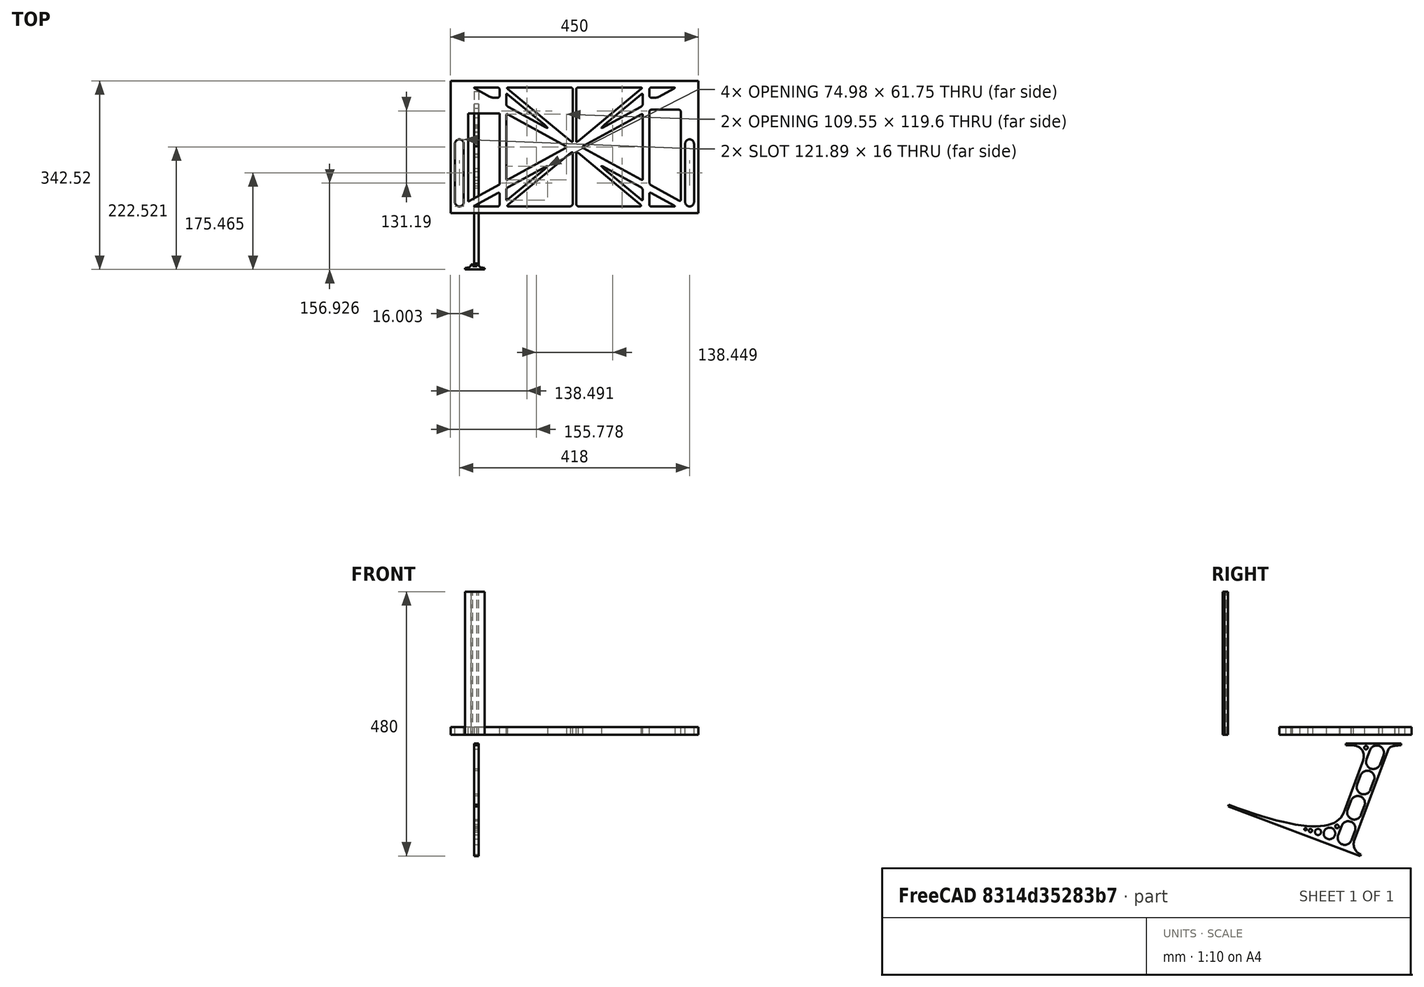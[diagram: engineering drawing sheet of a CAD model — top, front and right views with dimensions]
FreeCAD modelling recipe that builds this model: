
FCSTD DOCUMENT  (FreeCAD 0.19R0.19.2)
Label: laptopStand125FCStd
License: All rights reserved
LicenseURL: http://en.wikipedia.org/wiki/All_rights_reserved
objects: Sketcher::SketchObject×3, Part::Extrusion×3
note: 6 computed .brp shape members not serialized (recipe doc carries the construction recipe); baked Part::Feature solids carry a one-line shape summary decoded from their .brp

FEATURE [Sketcher::SketchObject] Sketch
  FullyConstrained = true
  sketch-geometry (351):
    g0: LineSegment StartX=-10.9272 StartY=-82.7794 StartZ=0 EndX=46.0728 EndY=-51.4823 EndZ=0
    g1: LineSegment StartX=-10.9272 StartY=77.3346 StartZ=0 EndX=-10.9272 EndY=-82.7794 EndZ=0
    g2: LineSegment StartX=46.0728 StartY=77.3346 StartZ=0 EndX=46.0728 EndY=-51.4823 EndZ=0
    g3: LineSegment StartX=-42.9272 StartY=136.221 StartZ=0 EndX=-42.9272 EndY=-103.779 EndZ=0
    g4: LineSegment StartX=407.073 StartY=136.221 StartZ=0 EndX=407.073 EndY=-103.779 EndZ=0
    g5: ArcOfCircle CenterX=-26.9272 CenterY=22.1087 CenterZ=0 NormalX=0 NormalY=0 NormalZ=1 AngleXU=0 Radius=8 StartAngle=1e-16 EndAngle=3.14159
    g6: ArcOfCircle CenterX=-26.9272 CenterY=-83.7794 CenterZ=0 NormalX=0 NormalY=0 NormalZ=1 AngleXU=0 Radius=8 StartAngle=3.14159 EndAngle=6.28319
    g7: LineSegment StartX=-34.9272 StartY=22.1087 StartZ=0 EndX=-34.9272 EndY=-83.7794 EndZ=0
    g8: LineSegment StartX=-18.9272 StartY=22.1087 StartZ=0 EndX=-18.9272 EndY=-83.7794 EndZ=0
    g9: ArcOfCircle CenterX=391.073 CenterY=22.1087 CenterZ=0 NormalX=0 NormalY=0 NormalZ=1 AngleXU=0 Radius=8 StartAngle=-4.4e-15 EndAngle=3.14159
    g10: LineSegment StartX=399.073 StartY=22.1087 StartZ=0 EndX=399.073 EndY=-83.7794 EndZ=0
    g11: LineSegment StartX=383.073 StartY=22.1087 StartZ=0 EndX=383.073 EndY=-83.7794 EndZ=0
    g12: ArcOfCircle CenterX=391.073 CenterY=-83.7794 CenterZ=0 NormalX=0 NormalY=0 NormalZ=1 AngleXU=0 Radius=8 StartAngle=3.14159 EndAngle=6.28319
    g13: Circle CenterX=175.022 CenterY=27.0628 CenterZ=0 NormalX=0 NormalY=0 NormalZ=1 AngleXU=0 Radius=1
    g14: Circle CenterX=179.022 CenterY=24.8665 CenterZ=0 NormalX=0 NormalY=0 NormalZ=1 AngleXU=0 Radius=1
    g15: Circle CenterX=179.022 CenterY=27.0628 CenterZ=0 NormalX=0 NormalY=0 NormalZ=1 AngleXU=0 Radius=1
    g16: BSplineCurve PolesCount=3 KnotsCount=2 Degree=2 IsPeriodic=0
    g17: GeomPoint X=175.022 Y=27.0628 Z=0
    g18: GeomPoint X=179.022 Y=27.0628 Z=0
    g19: Circle CenterX=189.124 CenterY=27.0628 CenterZ=0 NormalX=0 NormalY=0 NormalZ=1 AngleXU=0 Radius=1
    g20: Circle CenterX=185.124 CenterY=24.8665 CenterZ=0 NormalX=0 NormalY=0 NormalZ=1 AngleXU=0 Radius=1
    g21: Circle CenterX=185.124 CenterY=27.0628 CenterZ=0 NormalX=0 NormalY=0 NormalZ=1 AngleXU=0 Radius=1
    g22: BSplineCurve PolesCount=3 KnotsCount=2 Degree=2 IsPeriodic=0
    g23: GeomPoint X=189.124 Y=27.0628 Z=0
    g24: GeomPoint X=185.124 Y=27.0628 Z=0
    g25: Circle CenterX=175.022 CenterY=5.37834 CenterZ=0 NormalX=0 NormalY=0 NormalZ=1 AngleXU=0 Radius=1
    g26: Circle CenterX=179.022 CenterY=7.57463 CenterZ=0 NormalX=0 NormalY=0 NormalZ=1 AngleXU=0 Radius=1
    g27: Circle CenterX=179.022 CenterY=5.34704 CenterZ=0 NormalX=0 NormalY=0 NormalZ=1 AngleXU=0 Radius=1
    g28: BSplineCurve PolesCount=3 KnotsCount=2 Degree=2 IsPeriodic=0
    g29: GeomPoint X=175.022 Y=5.37834 Z=0
    g30: GeomPoint X=179.022 Y=5.34704 Z=0
    g31: Circle CenterX=189.124 CenterY=5.37834 CenterZ=0 NormalX=0 NormalY=0 NormalZ=1 AngleXU=0 Radius=1
    g32: Circle CenterX=185.124 CenterY=7.57463 CenterZ=0 NormalX=0 NormalY=0 NormalZ=1 AngleXU=0 Radius=1
    g33: Circle CenterX=185.124 CenterY=5.34704 CenterZ=0 NormalX=0 NormalY=0 NormalZ=1 AngleXU=0 Radius=1
    g34: BSplineCurve PolesCount=3 KnotsCount=2 Degree=2 IsPeriodic=0
    g35: GeomPoint X=189.124 Y=5.37834 Z=0
    g36: GeomPoint X=185.124 Y=5.34704 Z=0
    g37: Circle CenterX=165.871 CenterY=18.1458 CenterZ=0 NormalX=0 NormalY=0 NormalZ=1 AngleXU=0 Radius=1
    g38: Circle CenterX=169.377 CenterY=16.2206 CenterZ=0 NormalX=0 NormalY=0 NormalZ=1 AngleXU=0 Radius=1
    g39: Circle CenterX=165.871 CenterY=14.2954 CenterZ=0 NormalX=0 NormalY=0 NormalZ=1 AngleXU=0 Radius=1
    g40: BSplineCurve PolesCount=3 KnotsCount=2 Degree=2 IsPeriodic=0
    g41: GeomPoint X=165.871 Y=18.1458 Z=0
    g42: GeomPoint X=165.871 Y=14.2954 Z=0
    g43: Circle CenterX=198.275 CenterY=18.1458 CenterZ=0 NormalX=0 NormalY=0 NormalZ=1 AngleXU=0 Radius=1
    g44: Circle CenterX=194.768 CenterY=16.2206 CenterZ=0 NormalX=0 NormalY=0 NormalZ=1 AngleXU=0 Radius=1
    g45: Circle CenterX=198.275 CenterY=14.2954 CenterZ=0 NormalX=0 NormalY=0 NormalZ=1 AngleXU=0 Radius=1
    g46: BSplineCurve PolesCount=3 KnotsCount=2 Degree=2 IsPeriodic=0
    g47: GeomPoint X=198.275 Y=18.1458 Z=0
    g48: GeomPoint X=198.275 Y=14.2954 Z=0
    g49: LineSegment StartX=407.073 StartY=-103.779 StartZ=0 EndX=-42.9272 EndY=-103.779 EndZ=0
    g50: LineSegment StartX=407.073 StartY=136.221 StartZ=0 EndX=-42.9272 EndY=136.221 EndZ=0
    g51: LineSegment StartX=46.0728 StartY=77.3346 StartZ=0 EndX=-10.9272 EndY=77.3346 EndZ=0
    g52: Circle CenterX=125.607 CenterY=54.1951 CenterZ=0 NormalX=0 NormalY=0 NormalZ=1 AngleXU=0 Radius=1
    g53: Circle CenterX=139.632 CenterY=46.4944 CenterZ=0 NormalX=0 NormalY=0 NormalZ=1 AngleXU=0 Radius=1
    g54: Circle CenterX=127.326 CenterY=56.7187 CenterZ=0 NormalX=0 NormalY=0 NormalZ=1 AngleXU=0 Radius=1
    g55: BSplineCurve PolesCount=3 KnotsCount=2 Degree=2 IsPeriodic=0
    g56: GeomPoint X=125.607 Y=54.1951 Z=0
    g57: GeomPoint X=127.326 Y=56.7187 Z=0
    g58: Circle CenterX=236.821 CenterY=56.7187 CenterZ=0 NormalX=0 NormalY=0 NormalZ=1 AngleXU=0 Radius=1
    g59: Circle CenterX=224.513 CenterY=46.4944 CenterZ=0 NormalX=0 NormalY=0 NormalZ=1 AngleXU=0 Radius=1
    g60: Circle CenterX=238.538 CenterY=54.1951 CenterZ=0 NormalX=0 NormalY=0 NormalZ=1 AngleXU=0 Radius=1
    g61: BSplineCurve PolesCount=3 KnotsCount=2 Degree=2 IsPeriodic=0
    g62: GeomPoint X=236.821 Y=56.7187 Z=0
    g63: GeomPoint X=238.538 Y=54.1951 Z=0
    g64: Circle CenterX=238.538 CenterY=-21.7539 CenterZ=0 NormalX=0 NormalY=0 NormalZ=1 AngleXU=0 Radius=1
    g65: Circle CenterX=224.513 CenterY=-14.0532 CenterZ=0 NormalX=0 NormalY=0 NormalZ=1 AngleXU=0 Radius=1
    g66: Circle CenterX=236.821 CenterY=-24.2775 CenterZ=0 NormalX=0 NormalY=0 NormalZ=1 AngleXU=0 Radius=1
    g67: BSplineCurve PolesCount=3 KnotsCount=2 Degree=2 IsPeriodic=0
    g68: GeomPoint X=238.538 Y=-21.7539 Z=0
    g69: GeomPoint X=236.821 Y=-24.2775 Z=0
    g70: Circle CenterX=125.607 CenterY=-21.7539 CenterZ=0 NormalX=0 NormalY=0 NormalZ=1 AngleXU=0 Radius=1
    g71: Circle CenterX=139.632 CenterY=-14.0532 CenterZ=0 NormalX=0 NormalY=0 NormalZ=1 AngleXU=0 Radius=1
    g72: Circle CenterX=127.325 CenterY=-24.2775 CenterZ=0 NormalX=0 NormalY=0 NormalZ=1 AngleXU=0 Radius=1
    g73: BSplineCurve PolesCount=3 KnotsCount=2 Degree=2 IsPeriodic=0
    g74: GeomPoint X=125.607 Y=-21.7539 Z=0
    g75: GeomPoint X=127.325 Y=-24.2775 Z=0
    g76: Circle CenterX=302.996 CenterY=111.695 CenterZ=0 NormalX=0 NormalY=0 NormalZ=1 AngleXU=0 Radius=1
    g77: Circle CenterX=306.073 CenterY=114.251 CenterZ=0 NormalX=0 NormalY=0 NormalZ=1 AngleXU=0 Radius=1
    g78: Circle CenterX=306.073 CenterY=110.251 CenterZ=0 NormalX=0 NormalY=0 NormalZ=1 AngleXU=0 Radius=1
    g79: BSplineCurve PolesCount=3 KnotsCount=2 Degree=2 IsPeriodic=0
    g80: GeomPoint X=302.996 Y=111.695 Z=0
    g81: GeomPoint X=306.073 Y=110.251 Z=0
    g82: Circle CenterX=306.073 CenterY=95.2763 CenterZ=0 NormalX=0 NormalY=0 NormalZ=1 AngleXU=0 Radius=1
    g83: Circle CenterX=306.073 CenterY=91.2763 CenterZ=0 NormalX=0 NormalY=0 NormalZ=1 AngleXU=0 Radius=1
    g84: Circle CenterX=302.567 CenterY=89.3511 CenterZ=0 NormalX=0 NormalY=0 NormalZ=1 AngleXU=0 Radius=1
    g85: BSplineCurve PolesCount=3 KnotsCount=2 Degree=2 IsPeriodic=0
    g86: GeomPoint X=306.073 Y=95.2763 Z=0
    g87: GeomPoint X=302.567 Y=89.3511 Z=0
    g88: LineSegment StartX=306.073 StartY=110.251 StartZ=0 EndX=306.073 EndY=95.2763 EndZ=0
    g89: LineSegment StartX=302.996 StartY=111.695 StartZ=0 EndX=236.821 EndY=56.7187 EndZ=0
    g90: LineSegment StartX=238.538 StartY=54.1951 StartZ=0 EndX=302.567 EndY=89.3511 EndZ=0
    g91: Circle CenterX=61.1496 CenterY=111.695 CenterZ=0 NormalX=0 NormalY=0 NormalZ=1 AngleXU=0 Radius=1
    g92: Circle CenterX=58.0728 CenterY=114.251 CenterZ=0 NormalX=0 NormalY=0 NormalZ=1 AngleXU=0 Radius=1
    g93: Circle CenterX=58.0728 CenterY=110.251 CenterZ=0 NormalX=0 NormalY=0 NormalZ=1 AngleXU=0 Radius=1
    g94: BSplineCurve PolesCount=3 KnotsCount=2 Degree=2 IsPeriodic=0
    g95: GeomPoint X=61.1496 Y=111.695 Z=0
    g96: GeomPoint X=58.0728 Y=110.251 Z=0
    g97: Circle CenterX=61.5791 CenterY=89.3511 CenterZ=0 NormalX=0 NormalY=0 NormalZ=1 AngleXU=0 Radius=1
    g98: Circle CenterX=58.0728 CenterY=91.2763 CenterZ=0 NormalX=0 NormalY=0 NormalZ=1 AngleXU=0 Radius=1
    g99: Circle CenterX=58.0728 CenterY=95.2763 CenterZ=0 NormalX=0 NormalY=0 NormalZ=1 AngleXU=0 Radius=1
    g100: BSplineCurve PolesCount=3 KnotsCount=2 Degree=2 IsPeriodic=0
    g101: GeomPoint X=61.5791 Y=89.3511 Z=0
    g102: GeomPoint X=58.0728 Y=95.2763 Z=0
    g103: LineSegment StartX=58.0728 StartY=110.251 StartZ=0 EndX=58.0728 EndY=95.2763 EndZ=0
    g104: LineSegment StartX=61.1496 StartY=111.695 StartZ=0 EndX=127.326 EndY=56.7187 EndZ=0
    g105: LineSegment StartX=125.607 StartY=54.1951 StartZ=0 EndX=61.5791 EndY=89.3511 EndZ=0
    g106: Circle CenterX=61.5791 CenterY=-56.9099 CenterZ=0 NormalX=0 NormalY=0 NormalZ=1 AngleXU=0 Radius=1
    g107: Circle CenterX=58.0728 CenterY=-58.8351 CenterZ=0 NormalX=0 NormalY=0 NormalZ=1 AngleXU=0 Radius=1
    g108: Circle CenterX=58.0728 CenterY=-62.8351 CenterZ=0 NormalX=0 NormalY=0 NormalZ=1 AngleXU=0 Radius=1
    g109: BSplineCurve PolesCount=3 KnotsCount=2 Degree=2 IsPeriodic=0
    g110: GeomPoint X=61.5791 Y=-56.9099 Z=0
    g111: GeomPoint X=58.0728 Y=-62.8351 Z=0
    g112: Circle CenterX=58.0728 CenterY=-77.8102 CenterZ=0 NormalX=0 NormalY=0 NormalZ=1 AngleXU=0 Radius=1
    g113: Circle CenterX=58.0728 CenterY=-81.8102 CenterZ=0 NormalX=0 NormalY=0 NormalZ=1 AngleXU=0 Radius=1
    g114: Circle CenterX=61.1496 CenterY=-79.2541 CenterZ=0 NormalX=0 NormalY=0 NormalZ=1 AngleXU=0 Radius=1
    g115: BSplineCurve PolesCount=3 KnotsCount=2 Degree=2 IsPeriodic=0
    g116: GeomPoint X=58.0728 Y=-77.8102 Z=0
    g117: GeomPoint X=61.1496 Y=-79.2541 Z=0
    g118: LineSegment StartX=58.0728 StartY=-62.8351 StartZ=0 EndX=58.0728 EndY=-77.8102 EndZ=0
    g119: LineSegment StartX=61.1496 StartY=-79.2541 StartZ=0 EndX=127.325 EndY=-24.2775 EndZ=0
    g120: LineSegment StartX=125.607 StartY=-21.7539 StartZ=0 EndX=61.5791 EndY=-56.9099 EndZ=0
    g121: Circle CenterX=302.567 CenterY=-56.9099 CenterZ=0 NormalX=0 NormalY=0 NormalZ=1 AngleXU=0 Radius=1
    g122: Circle CenterX=306.073 CenterY=-58.8351 CenterZ=0 NormalX=0 NormalY=0 NormalZ=1 AngleXU=0 Radius=1
    g123: Circle CenterX=306.073 CenterY=-62.8351 CenterZ=0 NormalX=0 NormalY=0 NormalZ=1 AngleXU=0 Radius=1
    g124: BSplineCurve PolesCount=3 KnotsCount=2 Degree=2 IsPeriodic=0
    g125: GeomPoint X=302.567 Y=-56.9099 Z=0
    g126: GeomPoint X=306.073 Y=-62.8351 Z=0
    g127: Circle CenterX=302.996 CenterY=-79.2541 CenterZ=0 NormalX=0 NormalY=0 NormalZ=1 AngleXU=0 Radius=1
    g128: Circle CenterX=306.073 CenterY=-81.8102 CenterZ=0 NormalX=0 NormalY=0 NormalZ=1 AngleXU=0 Radius=1
    g129: Circle CenterX=306.073 CenterY=-77.8102 CenterZ=0 NormalX=0 NormalY=0 NormalZ=1 AngleXU=0 Radius=1
    g130: BSplineCurve PolesCount=3 KnotsCount=2 Degree=2 IsPeriodic=0
    g131: GeomPoint X=302.996 Y=-79.2541 Z=0
    g132: GeomPoint X=306.073 Y=-77.8102 Z=0
    g133: LineSegment StartX=306.073 StartY=-62.8351 StartZ=0 EndX=306.073 EndY=-77.8102 EndZ=0
    g134: LineSegment StartX=302.996 StartY=-79.2541 StartZ=0 EndX=236.821 EndY=-24.2775 EndZ=0
    g135: LineSegment StartX=238.538 StartY=-21.7539 StartZ=0 EndX=302.567 EndY=-56.9099 EndZ=0
    g136: Circle CenterX=61.6457 CenterY=-88.8112 CenterZ=0 NormalX=0 NormalY=0 NormalZ=1 AngleXU=0 Radius=1
    g137: Circle CenterX=58.0728 CenterY=-91.7794 CenterZ=0 NormalX=0 NormalY=0 NormalZ=1 AngleXU=0 Radius=1
    g138: Circle CenterX=63.9135 CenterY=-91.7794 CenterZ=0 NormalX=0 NormalY=0 NormalZ=1 AngleXU=0 Radius=1
    g139: BSplineCurve PolesCount=3 KnotsCount=2 Degree=2 IsPeriodic=0
    g140: GeomPoint X=61.6457 Y=-88.8112 Z=0
    g141: GeomPoint X=63.9135 Y=-91.7794 Z=0
    g142: Circle CenterX=179.022 CenterY=-85.8163 CenterZ=0 NormalX=0 NormalY=0 NormalZ=1 AngleXU=0 Radius=1
    g143: Circle CenterX=179.022 CenterY=-91.7794 CenterZ=0 NormalX=0 NormalY=0 NormalZ=1 AngleXU=0 Radius=1
    g144: Circle CenterX=171.895 CenterY=-91.7794 CenterZ=0 NormalX=0 NormalY=0 NormalZ=1 AngleXU=0 Radius=1
    g145: BSplineCurve PolesCount=3 KnotsCount=2 Degree=2 IsPeriodic=0
    g146: GeomPoint X=179.022 Y=-85.8163 Z=0
    g147: GeomPoint X=171.895 Y=-91.7794 Z=0
    g148: Circle CenterX=185.124 CenterY=-86.2028 CenterZ=0 NormalX=0 NormalY=0 NormalZ=1 AngleXU=0 Radius=1
    g149: Circle CenterX=185.124 CenterY=-91.7794 CenterZ=0 NormalX=0 NormalY=0 NormalZ=1 AngleXU=0 Radius=1
    g150: Circle CenterX=191.747 CenterY=-91.7794 CenterZ=0 NormalX=0 NormalY=0 NormalZ=1 AngleXU=0 Radius=1
    g151: BSplineCurve PolesCount=3 KnotsCount=2 Degree=2 IsPeriodic=0
    g152: GeomPoint X=185.124 Y=-86.2028 Z=0
    g153: GeomPoint X=191.747 Y=-91.7794 Z=0
    g154: Circle CenterX=299.888 CenterY=-86.6413 CenterZ=0 NormalX=0 NormalY=0 NormalZ=1 AngleXU=0 Radius=1
    g155: Circle CenterX=306.073 CenterY=-91.7794 CenterZ=0 NormalX=0 NormalY=0 NormalZ=1 AngleXU=0 Radius=1
    g156: Circle CenterX=298.776 CenterY=-91.7794 CenterZ=0 NormalX=0 NormalY=0 NormalZ=1 AngleXU=0 Radius=1
    g157: BSplineCurve PolesCount=3 KnotsCount=2 Degree=2 IsPeriodic=0
    g158: GeomPoint X=299.888 Y=-86.6413 Z=0
    g159: GeomPoint X=298.776 Y=-91.7794 Z=0
    g160: LineSegment StartX=189.124 StartY=5.37834 StartZ=0 EndX=299.888 EndY=-86.6413 EndZ=0
    g161: LineSegment StartX=298.776 StartY=-91.7794 StartZ=0 EndX=191.747 EndY=-91.7794 EndZ=0
    g162: LineSegment StartX=185.124 StartY=-86.2028 StartZ=0 EndX=185.124 EndY=5.34704 EndZ=0
    g163: LineSegment StartX=179.022 StartY=5.34704 StartZ=0 EndX=179.022 EndY=-85.8163 EndZ=0
    g164: LineSegment StartX=171.895 StartY=-91.7794 StartZ=0 EndX=63.9135 EndY=-91.7794 EndZ=0
    g165: LineSegment StartX=61.6457 StartY=-88.8112 StartZ=0 EndX=175.022 EndY=5.37834 EndZ=0
    g166: Circle CenterX=302.073 CenterY=124.221 CenterZ=0 NormalX=0 NormalY=0 NormalZ=1 AngleXU=0 Radius=1
    g167: Circle CenterX=306.073 CenterY=124.221 CenterZ=0 NormalX=0 NormalY=0 NormalZ=1 AngleXU=0 Radius=1
    g168: Circle CenterX=302.996 CenterY=121.665 CenterZ=0 NormalX=0 NormalY=0 NormalZ=1 AngleXU=0 Radius=1
    g169: BSplineCurve PolesCount=3 KnotsCount=2 Degree=2 IsPeriodic=0
    g170: GeomPoint X=302.073 Y=124.221 Z=0
    g171: GeomPoint X=302.996 Y=121.665 Z=0
    g172: Circle CenterX=189.124 CenterY=124.221 CenterZ=0 NormalX=0 NormalY=0 NormalZ=1 AngleXU=0 Radius=1
    g173: Circle CenterX=185.124 CenterY=124.221 CenterZ=0 NormalX=0 NormalY=0 NormalZ=1 AngleXU=0 Radius=1
    g174: Circle CenterX=185.124 CenterY=120.221 CenterZ=0 NormalX=0 NormalY=0 NormalZ=1 AngleXU=0 Radius=1
    g175: BSplineCurve PolesCount=3 KnotsCount=2 Degree=2 IsPeriodic=0
    g176: GeomPoint X=189.124 Y=124.221 Z=0
    g177: GeomPoint X=185.124 Y=120.221 Z=0
    g178: Circle CenterX=175.022 CenterY=124.221 CenterZ=0 NormalX=0 NormalY=0 NormalZ=1 AngleXU=0 Radius=1
    g179: Circle CenterX=179.022 CenterY=124.221 CenterZ=0 NormalX=0 NormalY=0 NormalZ=1 AngleXU=0 Radius=1
    g180: Circle CenterX=179.022 CenterY=120.221 CenterZ=0 NormalX=0 NormalY=0 NormalZ=1 AngleXU=0 Radius=1
    g181: BSplineCurve PolesCount=3 KnotsCount=2 Degree=2 IsPeriodic=0
    g182: GeomPoint X=175.022 Y=124.221 Z=0
    g183: GeomPoint X=179.022 Y=120.221 Z=0
    g184: Circle CenterX=62.0728 CenterY=124.221 CenterZ=0 NormalX=0 NormalY=0 NormalZ=1 AngleXU=0 Radius=1
    g185: Circle CenterX=58.0728 CenterY=124.221 CenterZ=0 NormalX=0 NormalY=0 NormalZ=1 AngleXU=0 Radius=1
    g186: Circle CenterX=61.1496 CenterY=121.665 CenterZ=0 NormalX=0 NormalY=0 NormalZ=1 AngleXU=0 Radius=1
    g187: BSplineCurve PolesCount=3 KnotsCount=2 Degree=2 IsPeriodic=0
    g188: GeomPoint X=62.0728 Y=124.221 Z=0
    g189: GeomPoint X=61.1496 Y=121.665 Z=0
    g190: LineSegment StartX=62.0728 StartY=124.221 StartZ=0 EndX=175.022 EndY=124.221 EndZ=0
    g191: LineSegment StartX=179.022 StartY=120.221 StartZ=0 EndX=179.022 EndY=27.0628 EndZ=0
    g192: LineSegment StartX=185.124 StartY=27.0628 StartZ=0 EndX=185.124 EndY=120.221 EndZ=0
    g193: LineSegment StartX=189.124 StartY=124.221 StartZ=0 EndX=302.073 EndY=124.221 EndZ=0
    g194: LineSegment StartX=302.996 StartY=121.665 StartZ=0 EndX=189.124 EndY=27.0628 EndZ=0
    g195: LineSegment StartX=175.022 StartY=27.0628 StartZ=0 EndX=61.1496 EndY=121.665 EndZ=0
    g196: Circle CenterX=61.5791 CenterY=75.4095 CenterZ=0 NormalX=0 NormalY=0 NormalZ=1 AngleXU=0 Radius=1
    g197: Circle CenterX=58.0728 CenterY=77.3346 CenterZ=0 NormalX=0 NormalY=0 NormalZ=1 AngleXU=0 Radius=1
    g198: Circle CenterX=58.0728 CenterY=73.3346 CenterZ=0 NormalX=0 NormalY=0 NormalZ=1 AngleXU=0 Radius=1
    g199: BSplineCurve PolesCount=3 KnotsCount=2 Degree=2 IsPeriodic=0
    g200: GeomPoint X=61.5791 Y=75.4095 Z=0
    g201: GeomPoint X=58.0728 Y=73.3346 Z=0
    g202: Circle CenterX=58.0728 CenterY=-40.8935 CenterZ=0 NormalX=0 NormalY=0 NormalZ=1 AngleXU=0 Radius=1
    g203: Circle CenterX=58.0728 CenterY=-44.8935 CenterZ=0 NormalX=0 NormalY=0 NormalZ=1 AngleXU=0 Radius=1
    g204: Circle CenterX=61.5791 CenterY=-42.9683 CenterZ=0 NormalX=0 NormalY=0 NormalZ=1 AngleXU=0 Radius=1
    g205: BSplineCurve PolesCount=3 KnotsCount=2 Degree=2 IsPeriodic=0
    g206: GeomPoint X=58.0728 Y=-40.8935 Z=0
    g207: GeomPoint X=61.5791 Y=-42.9683 Z=0
    g208: LineSegment StartX=61.5791 StartY=-42.9683 StartZ=0 EndX=165.871 EndY=14.2954 EndZ=0
    g209: LineSegment StartX=165.871 StartY=18.1458 StartZ=0 EndX=61.5791 EndY=75.4095 EndZ=0
    g210: LineSegment StartX=58.0728 StartY=73.3346 StartZ=0 EndX=58.0728 EndY=-40.8935 EndZ=0
    g211: Circle CenterX=302.567 CenterY=-42.9683 CenterZ=0 NormalX=0 NormalY=0 NormalZ=1 AngleXU=0 Radius=1
    g212: Circle CenterX=306.073 CenterY=-44.8935 CenterZ=0 NormalX=0 NormalY=0 NormalZ=1 AngleXU=0 Radius=1
    g213: Circle CenterX=306.073 CenterY=-40.8935 CenterZ=0 NormalX=0 NormalY=0 NormalZ=1 AngleXU=0 Radius=1
    g214: BSplineCurve PolesCount=3 KnotsCount=2 Degree=2 IsPeriodic=0
    g215: GeomPoint X=302.567 Y=-42.9683 Z=0
    g216: GeomPoint X=306.073 Y=-40.8935 Z=0
    g217: Circle CenterX=306.073 CenterY=73.3346 CenterZ=0 NormalX=0 NormalY=0 NormalZ=1 AngleXU=0 Radius=1
    g218: Circle CenterX=306.073 CenterY=77.3346 CenterZ=0 NormalX=0 NormalY=0 NormalZ=1 AngleXU=0 Radius=1
    g219: Circle CenterX=302.567 CenterY=75.4095 CenterZ=0 NormalX=0 NormalY=0 NormalZ=1 AngleXU=0 Radius=1
    g220: BSplineCurve PolesCount=3 KnotsCount=2 Degree=2 IsPeriodic=0
    g221: GeomPoint X=306.073 Y=73.3346 Z=0
    g222: GeomPoint X=302.567 Y=75.4095 Z=0
    g223: LineSegment StartX=302.567 StartY=-42.9683 StartZ=0 EndX=198.275 EndY=14.2954 EndZ=0
    g224: LineSegment StartX=198.275 StartY=18.1458 StartZ=0 EndX=302.567 EndY=75.4095 EndZ=0
    g225: LineSegment StartX=306.073 StartY=73.3346 StartZ=0 EndX=306.073 EndY=-40.8935 EndZ=0
    g226: LineSegment StartX=322.073 StartY=105.865 StartZ=0 EndX=328.643 EndY=105.865 EndZ=0
    g227: LineSegment StartX=318.073 StartY=120.221 StartZ=0 EndX=318.073 EndY=109.865 EndZ=0
    g228: LineSegment StartX=336.157 StartY=107.779 StartZ=0 EndX=362.567 EndY=122.294 EndZ=0
    g229: Circle CenterX=362.073 CenterY=124.221 CenterZ=0 NormalX=0 NormalY=0 NormalZ=1 AngleXU=0 Radius=1
    g230: Circle CenterX=366.073 CenterY=124.221 CenterZ=0 NormalX=0 NormalY=0 NormalZ=1 AngleXU=0 Radius=1
    g231: Circle CenterX=362.567 CenterY=122.294 CenterZ=0 NormalX=0 NormalY=0 NormalZ=1 AngleXU=0 Radius=1
    g232: BSplineCurve PolesCount=3 KnotsCount=2 Degree=2 IsPeriodic=0
    g233: GeomPoint X=362.073 Y=124.221 Z=0
    g234: GeomPoint X=362.567 Y=122.294 Z=0
    g235: Circle CenterX=322.073 CenterY=124.221 CenterZ=0 NormalX=0 NormalY=0 NormalZ=1 AngleXU=0 Radius=1
    g236: Circle CenterX=318.073 CenterY=124.221 CenterZ=0 NormalX=0 NormalY=0 NormalZ=1 AngleXU=0 Radius=1
    g237: Circle CenterX=318.073 CenterY=120.221 CenterZ=0 NormalX=0 NormalY=0 NormalZ=1 AngleXU=0 Radius=1
    g238: BSplineCurve PolesCount=3 KnotsCount=2 Degree=2 IsPeriodic=0
    g239: GeomPoint X=322.073 Y=124.221 Z=0
    g240: GeomPoint X=318.073 Y=120.221 Z=0
    g241: Circle CenterX=322.073 CenterY=105.865 CenterZ=0 NormalX=0 NormalY=0 NormalZ=1 AngleXU=0 Radius=1
    g242: Circle CenterX=318.073 CenterY=105.865 CenterZ=0 NormalX=0 NormalY=0 NormalZ=1 AngleXU=0 Radius=1
    g243: Circle CenterX=318.073 CenterY=109.865 CenterZ=0 NormalX=0 NormalY=0 NormalZ=1 AngleXU=0 Radius=1
    g244: BSplineCurve PolesCount=3 KnotsCount=2 Degree=2 IsPeriodic=0
    g245: GeomPoint X=322.073 Y=105.865 Z=0
    g246: GeomPoint X=318.073 Y=109.865 Z=0
    g247: Circle CenterX=336.157 CenterY=107.779 CenterZ=0 NormalX=0 NormalY=0 NormalZ=1 AngleXU=0 Radius=1
    g248: Circle CenterX=332.651 CenterY=105.853 CenterZ=0 NormalX=0 NormalY=0 NormalZ=1 AngleXU=0 Radius=1
    g249: Circle CenterX=328.643 CenterY=105.865 CenterZ=0 NormalX=0 NormalY=0 NormalZ=1 AngleXU=0 Radius=1
    g250: BSplineCurve PolesCount=3 KnotsCount=2 Degree=2 IsPeriodic=0
    g251: GeomPoint X=336.157 Y=107.779 Z=0
    g252: GeomPoint X=328.643 Y=105.865 Z=0
    g253: LineSegment StartX=322.073 StartY=124.221 StartZ=0 EndX=362.073 EndY=124.221 EndZ=0
    g254: Circle CenterX=371.567 CenterY=-80.8644 CenterZ=0 NormalX=0 NormalY=0 NormalZ=1 AngleXU=0 Radius=1
    g255: Circle CenterX=375.073 CenterY=-82.7896 CenterZ=0 NormalX=0 NormalY=0 NormalZ=1 AngleXU=0 Radius=1
    g256: Circle CenterX=375.073 CenterY=-78.7896 CenterZ=0 NormalX=0 NormalY=0 NormalZ=1 AngleXU=0 Radius=1
    g257: BSplineCurve PolesCount=3 KnotsCount=2 Degree=2 IsPeriodic=0
    g258: GeomPoint X=371.567 Y=-80.8644 Z=0
    g259: GeomPoint X=375.073 Y=-78.7896 Z=0
    g260: Circle CenterX=321.579 CenterY=-53.4075 CenterZ=0 NormalX=0 NormalY=0 NormalZ=1 AngleXU=0 Radius=1
    g261: Circle CenterX=318.073 CenterY=-51.4823 CenterZ=0 NormalX=0 NormalY=0 NormalZ=1 AngleXU=0 Radius=1
    g262: Circle CenterX=318.073 CenterY=-47.4823 CenterZ=0 NormalX=0 NormalY=0 NormalZ=1 AngleXU=0 Radius=1
    g263: BSplineCurve PolesCount=3 KnotsCount=2 Degree=2 IsPeriodic=0
    g264: GeomPoint X=321.579 Y=-53.4075 Z=0
    g265: GeomPoint X=318.073 Y=-47.4823 Z=0
    g266: Circle CenterX=318.073 CenterY=79.9235 CenterZ=0 NormalX=0 NormalY=0 NormalZ=1 AngleXU=0 Radius=1
    g267: Circle CenterX=318.073 CenterY=83.9235 CenterZ=0 NormalX=0 NormalY=0 NormalZ=1 AngleXU=0 Radius=1
    g268: Circle CenterX=322.073 CenterY=83.9235 CenterZ=0 NormalX=0 NormalY=0 NormalZ=1 AngleXU=0 Radius=1
    g269: BSplineCurve PolesCount=3 KnotsCount=2 Degree=2 IsPeriodic=0
    g270: GeomPoint X=318.073 Y=79.9235 Z=0
    g271: GeomPoint X=322.073 Y=83.9235 Z=0
    g272: Circle CenterX=375.073 CenterY=79.9235 CenterZ=0 NormalX=0 NormalY=0 NormalZ=1 AngleXU=0 Radius=1
    g273: Circle CenterX=375.073 CenterY=83.9235 CenterZ=0 NormalX=0 NormalY=0 NormalZ=1 AngleXU=0 Radius=1
    g274: Circle CenterX=371.073 CenterY=83.9235 CenterZ=0 NormalX=0 NormalY=0 NormalZ=1 AngleXU=0 Radius=1
    g275: BSplineCurve PolesCount=3 KnotsCount=2 Degree=2 IsPeriodic=0
    g276: GeomPoint X=375.073 Y=79.9235 Z=0
    g277: GeomPoint X=371.073 Y=83.9235 Z=0
    g278: LineSegment StartX=322.073 StartY=83.9235 StartZ=0 EndX=371.073 EndY=83.9235 EndZ=0
    g279: LineSegment StartX=375.073 StartY=79.9235 StartZ=0 EndX=375.073 EndY=-78.7896 EndZ=0
    g280: LineSegment StartX=371.567 StartY=-80.8644 StartZ=0 EndX=321.579 EndY=-53.4075 EndZ=0
    g281: LineSegment StartX=318.073 StartY=-47.4823 StartZ=0 EndX=318.073 EndY=79.9235 EndZ=0
    g282: Circle CenterX=321.579 CenterY=-67.3492 CenterZ=0 NormalX=0 NormalY=0 NormalZ=1 AngleXU=0 Radius=1
    g283: Circle CenterX=318.073 CenterY=-65.424 CenterZ=0 NormalX=0 NormalY=0 NormalZ=1 AngleXU=0 Radius=1
    g284: Circle CenterX=318.073 CenterY=-69.424 CenterZ=0 NormalX=0 NormalY=0 NormalZ=1 AngleXU=0 Radius=1
    g285: BSplineCurve PolesCount=3 KnotsCount=2 Degree=2 IsPeriodic=0
    g286: GeomPoint X=321.579 Y=-67.3492 Z=0
    g287: GeomPoint X=318.073 Y=-69.424 Z=0
    g288: Circle CenterX=362.567 CenterY=-89.8542 CenterZ=0 NormalX=0 NormalY=0 NormalZ=1 AngleXU=0 Radius=1
    g289: Circle CenterX=366.073 CenterY=-91.7794 CenterZ=0 NormalX=0 NormalY=0 NormalZ=1 AngleXU=0 Radius=1
    g290: Circle CenterX=362.073 CenterY=-91.7794 CenterZ=0 NormalX=0 NormalY=0 NormalZ=1 AngleXU=0 Radius=1
    g291: BSplineCurve PolesCount=3 KnotsCount=2 Degree=2 IsPeriodic=0
    g292: GeomPoint X=362.567 Y=-89.8542 Z=0
    g293: GeomPoint X=362.073 Y=-91.7794 Z=0
    g294: Circle CenterX=322.073 CenterY=-91.7794 CenterZ=0 NormalX=0 NormalY=0 NormalZ=1 AngleXU=0 Radius=1
    g295: Circle CenterX=318.073 CenterY=-91.7794 CenterZ=0 NormalX=0 NormalY=0 NormalZ=1 AngleXU=0 Radius=1
    g296: Circle CenterX=318.073 CenterY=-87.7794 CenterZ=0 NormalX=0 NormalY=0 NormalZ=1 AngleXU=0 Radius=1
    g297: BSplineCurve PolesCount=3 KnotsCount=2 Degree=2 IsPeriodic=0
    g298: GeomPoint X=322.073 Y=-91.7794 Z=0
    g299: GeomPoint X=318.073 Y=-87.7794 Z=0
    g300: LineSegment StartX=362.567 StartY=-89.8542 StartZ=0 EndX=321.579 EndY=-67.3492 EndZ=0
    g301: LineSegment StartX=318.073 StartY=-69.424 StartZ=0 EndX=318.073 EndY=-87.7794 EndZ=0
    g302: LineSegment StartX=322.073 StartY=-91.7794 StartZ=0 EndX=362.073 EndY=-91.7794 EndZ=0
    g303: Circle CenterX=2.07281 CenterY=124.221 CenterZ=0 NormalX=0 NormalY=0 NormalZ=1 AngleXU=0 Radius=1
    g304: Circle CenterX=1.57905 CenterY=122.295 CenterZ=0 NormalX=0 NormalY=0 NormalZ=1 AngleXU=0 Radius=1
    g305: BSplineCurve PolesCount=3 KnotsCount=2 Degree=2 IsPeriodic=0
    g306: GeomPoint X=2.07281 Y=124.221 Z=0
    g307: GeomPoint X=1.57905 Y=122.295 Z=0
    g308: Circle CenterX=42.0728 CenterY=124.221 CenterZ=0 NormalX=0 NormalY=0 NormalZ=1 AngleXU=0 Radius=1
    g309: Circle CenterX=46.0728 CenterY=124.221 CenterZ=0 NormalX=0 NormalY=0 NormalZ=1 AngleXU=0 Radius=1
    g310: Circle CenterX=46.0728 CenterY=120.221 CenterZ=0 NormalX=0 NormalY=0 NormalZ=1 AngleXU=0 Radius=1
    g311: BSplineCurve PolesCount=3 KnotsCount=2 Degree=2 IsPeriodic=0
    g312: GeomPoint X=42.0728 Y=124.221 Z=0
    g313: GeomPoint X=46.0728 Y=120.221 Z=0
    g314: Circle CenterX=46.0728 CenterY=109.865 CenterZ=0 NormalX=0 NormalY=0 NormalZ=1 AngleXU=0 Radius=1
    g315: Circle CenterX=46.0728 CenterY=105.865 CenterZ=0 NormalX=0 NormalY=0 NormalZ=1 AngleXU=0 Radius=1
    g316: Circle CenterX=42.0728 CenterY=105.865 CenterZ=0 NormalX=0 NormalY=0 NormalZ=1 AngleXU=0 Radius=1
    g317: BSplineCurve PolesCount=3 KnotsCount=2 Degree=2 IsPeriodic=0
    g318: GeomPoint X=46.0728 Y=109.865 Z=0
    g319: GeomPoint X=42.0728 Y=105.865 Z=0
    g320: Circle CenterX=35.5028 CenterY=105.865 CenterZ=0 NormalX=0 NormalY=0 NormalZ=1 AngleXU=0 Radius=1
    g321: Circle CenterX=31.5028 CenterY=105.865 CenterZ=0 NormalX=0 NormalY=0 NormalZ=1 AngleXU=0 Radius=1
    g322: Circle CenterX=27.9965 CenterY=107.79 CenterZ=0 NormalX=0 NormalY=0 NormalZ=1 AngleXU=0 Radius=1
    g323: BSplineCurve PolesCount=3 KnotsCount=2 Degree=2 IsPeriodic=0
    g324: GeomPoint X=35.5028 Y=105.865 Z=0
    g325: GeomPoint X=27.9965 Y=107.79 Z=0
    g326: LineSegment StartX=2.07281 StartY=124.221 StartZ=0 EndX=42.0728 EndY=124.221 EndZ=0
    g327: LineSegment StartX=46.0728 StartY=120.221 StartZ=0 EndX=46.0728 EndY=109.865 EndZ=0
    g328: LineSegment StartX=42.0728 StartY=105.865 StartZ=0 EndX=35.5028 EndY=105.865 EndZ=0
    g329: LineSegment StartX=27.9965 StartY=107.79 StartZ=0 EndX=1.57905 EndY=122.295 EndZ=0
    g330: Circle CenterX=42.5666 CenterY=-67.3492 CenterZ=0 NormalX=0 NormalY=0 NormalZ=1 AngleXU=0 Radius=1
    g331: Circle CenterX=46.0728 CenterY=-65.424 CenterZ=0 NormalX=0 NormalY=0 NormalZ=1 AngleXU=0 Radius=1
    g332: Circle CenterX=46.0728 CenterY=-69.424 CenterZ=0 NormalX=0 NormalY=0 NormalZ=1 AngleXU=0 Radius=1
    g333: BSplineCurve PolesCount=3 KnotsCount=2 Degree=2 IsPeriodic=0
    g334: GeomPoint X=42.5666 Y=-67.3492 Z=0
    g335: GeomPoint X=46.0728 Y=-69.424 Z=0
    g336: Circle CenterX=46.0728 CenterY=-87.7794 CenterZ=0 NormalX=0 NormalY=0 NormalZ=1 AngleXU=0 Radius=1
    g337: Circle CenterX=46.0728 CenterY=-91.7794 CenterZ=0 NormalX=0 NormalY=0 NormalZ=1 AngleXU=0 Radius=1
    g338: Circle CenterX=42.0728 CenterY=-91.7794 CenterZ=0 NormalX=0 NormalY=0 NormalZ=1 AngleXU=0 Radius=1
    g339: BSplineCurve PolesCount=3 KnotsCount=2 Degree=2 IsPeriodic=0
    g340: GeomPoint X=46.0728 Y=-87.7794 Z=0
    g341: GeomPoint X=42.0728 Y=-91.7794 Z=0
    g342: Circle CenterX=2.07281 CenterY=-91.7794 CenterZ=0 NormalX=0 NormalY=0 NormalZ=1 AngleXU=0 Radius=1
    g343: Circle CenterX=-1.92719 CenterY=-91.7794 CenterZ=0 NormalX=0 NormalY=0 NormalZ=1 AngleXU=0 Radius=1
    g344: Circle CenterX=1.57905 CenterY=-89.8542 CenterZ=0 NormalX=0 NormalY=0 NormalZ=1 AngleXU=0 Radius=1
    g345: BSplineCurve PolesCount=3 KnotsCount=2 Degree=2 IsPeriodic=0
    g346: GeomPoint X=2.07281 Y=-91.7794 Z=0
    g347: GeomPoint X=1.57905 Y=-89.8542 Z=0
    g348: LineSegment StartX=2.07281 StartY=-91.7794 StartZ=0 EndX=42.0728 EndY=-91.7794 EndZ=0
    g349: LineSegment StartX=46.0728 StartY=-87.7794 StartZ=0 EndX=46.0728 EndY=-69.424 EndZ=0
    g350: LineSegment StartX=42.5666 StartY=-67.3492 StartZ=0 EndX=1.57905 EndY=-89.8542 EndZ=0
  constraints (582):
    c: Coincident(g0,g2)
    c: Block(g0)
    c: Block(g1)
    c: Vertical(g3)
    c: Vertical(g4)
    c: Block(g4)
    c: Block(g3)
    c: Tangent(g5,g8) = 1.5708
    c: Tangent(g5,g7) = -1.5708
    c: Tangent(g7,g6) = -1.5708
    c: Tangent(g8,g6) = 1.5708
    c: Vertical(g7)
    c: Equal(g5,g6)
    c: Block(g8)
    c: Block(g7)
    c: Tangent(g9,g10) = 1.5708
    c: Tangent(g10,g12) = 1.5708
    c: Equal(g9,g12)
    c: Coincident(g11,g9)
    c: Coincident(g11,g12)
    c: Block(g10)
    c: Block(g11)
    c: Weight(g13) = 1
    c: Equal(g13,g14)
    c: Equal(g13,g15)
    c: InternalAlignment(g13,g16)
    c: InternalAlignment(g14,g16)
    c: InternalAlignment(g15,g16)
    c: InternalAlignment(g17,g16)
    c: InternalAlignment(g18,g16)
    c: Weight(g19) = 1
    c: Equal(g19,g20)
    c: Equal(g19,g21)
    c: InternalAlignment(g19,g22)
    c: InternalAlignment(g20,g22)
    c: InternalAlignment(g21,g22)
    c: InternalAlignment(g23,g22)
    c: InternalAlignment(g24,g22)
    c: Block(g22)
    c: Block(g16)
    c: Weight(g25) = 1
    c: Equal(g25,g26)
    c: Equal(g25,g27)
    c: InternalAlignment(g25,g28)
    c: InternalAlignment(g26,g28)
    c: InternalAlignment(g27,g28)
    c: InternalAlignment(g29,g28)
    c: InternalAlignment(g30,g28)
    c: Weight(g31) = 1
    c: Equal(g31,g32)
    c: Equal(g31,g33)
    c: InternalAlignment(g31,g34)
    c: InternalAlignment(g32,g34)
    c: InternalAlignment(g33,g34)
    c: InternalAlignment(g35,g34)
    c: InternalAlignment(g36,g34)
    c: Block(g34)
    c: Block(g28)
    c: Weight(g37) = 1
    c: Equal(g37,g38)
    c: Equal(g37,g39)
    c: InternalAlignment(g37,g40)
    c: InternalAlignment(g38,g40)
    c: InternalAlignment(g39,g40)
    c: InternalAlignment(g41,g40)
    c: InternalAlignment(g42,g40)
    c: Weight(g43) = 1
    c: Equal(g43,g44)
    c: Equal(g43,g45)
    c: InternalAlignment(g43,g46)
    c: InternalAlignment(g44,g46)
    c: InternalAlignment(g45,g46)
    c: InternalAlignment(g47,g46)
    c: InternalAlignment(g48,g46)
    c: Block(g40)
    c: Block(g46)
    c: Coincident(g49,g4)
    c: Coincident(g49,g3)
    c: Horizontal(g49)
    c: Distance(g49) = 450
    c: Coincident(g50,g4)
    c: Coincident(g50,g3)
    c: Horizontal(g50)
    c: Horizontal(g51)
    c: Coincident(g2,g51)
    c: Block(g51)
    c: Coincident(g1,g51)
    c: Weight(g52) = 1
    c: Equal(g52,g53)
    c: Equal(g52,g54)
    c: InternalAlignment(g52,g55)
    c: InternalAlignment(g53,g55)
    c: InternalAlignment(g54,g55)
    c: InternalAlignment(g56,g55)
    c: InternalAlignment(g57,g55)
    c: Block(g55)
    c: Weight(g58) = 1
    c: Equal(g58,g59)
    c: Equal(g58,g60)
    c: InternalAlignment(g58,g61)
    c: InternalAlignment(g59,g61)
    c: InternalAlignment(g60,g61)
    c: InternalAlignment(g62,g61)
    c: InternalAlignment(g63,g61)
    c: Block(g61)
    c: Weight(g64) = 1
    c: Equal(g64,g65)
    c: Equal(g64,g66)
    c: InternalAlignment(g64,g67)
    c: InternalAlignment(g65,g67)
    c: InternalAlignment(g66,g67)
    c: InternalAlignment(g68,g67)
    c: InternalAlignment(g69,g67)
    c: Block(g67)
    c: Weight(g70) = 1
    c: Equal(g70,g71)
    c: Equal(g70,g72)
    c: InternalAlignment(g70,g73)
    c: InternalAlignment(g71,g73)
    c: InternalAlignment(g72,g73)
    c: InternalAlignment(g74,g73)
    c: InternalAlignment(g75,g73)
    c: Block(g73)
    c: Weight(g76) = 1
    c: Equal(g76,g77)
    c: Equal(g76,g78)
    c: InternalAlignment(g76,g79)
    c: InternalAlignment(g77,g79)
    c: InternalAlignment(g78,g79)
    c: InternalAlignment(g80,g79)
    c: InternalAlignment(g81,g79)
    c: Weight(g82) = 1
    c: Equal(g82,g83)
    c: Equal(g82,g84)
    c: InternalAlignment(g82,g85)
    c: InternalAlignment(g83,g85)
    c: InternalAlignment(g84,g85)
    c: InternalAlignment(g86,g85)
    c: InternalAlignment(g87,g85)
    c: Block(g79)
    c: Block(g85)
    c: Coincident(g88,g79)
    c: Coincident(g88,g85)
    c: Vertical(g88)
    c: Coincident(g89,g79)
    c: Coincident(g89,g61)
    c: Coincident(g90,g61)
    c: Coincident(g90,g85)
    c: Weight(g91) = 1
    c: Equal(g91,g92)
    c: Equal(g91,g93)
    c: InternalAlignment(g91,g94)
    c: InternalAlignment(g92,g94)
    c: InternalAlignment(g93,g94)
    c: InternalAlignment(g95,g94)
    c: InternalAlignment(g96,g94)
    c: Weight(g97) = 1
    c: Equal(g97,g98)
    c: Equal(g97,g99)
    c: InternalAlignment(g97,g100)
    c: InternalAlignment(g98,g100)
    c: InternalAlignment(g99,g100)
    c: InternalAlignment(g101,g100)
    c: InternalAlignment(g102,g100)
    c: Block(g94)
    c: Block(g100)
    c: Coincident(g103,g94)
    c: Coincident(g103,g100)
    c: Vertical(g103)
    c: Coincident(g104,g94)
    c: Coincident(g104,g55)
    c: Coincident(g105,g55)
    c: Coincident(g105,g100)
    c: Weight(g106) = 1
    c: Equal(g106,g107)
    c: Equal(g106,g108)
    c: InternalAlignment(g106,g109)
    c: InternalAlignment(g107,g109)
    c: InternalAlignment(g108,g109)
    c: InternalAlignment(g110,g109)
    c: InternalAlignment(g111,g109)
    c: Weight(g112) = 1
    c: Equal(g112,g113)
    c: Equal(g112,g114)
    c: InternalAlignment(g112,g115)
    c: InternalAlignment(g113,g115)
    c: InternalAlignment(g114,g115)
    c: InternalAlignment(g116,g115)
    c: InternalAlignment(g117,g115)
    c: Block(g109)
    c: Block(g115)
    c: Coincident(g118,g109)
    c: Coincident(g118,g115)
    c: Vertical(g118)
    c: Coincident(g119,g115)
    c: Coincident(g119,g73)
    c: Coincident(g120,g73)
    c: Coincident(g120,g109)
    c: Weight(g121) = 1
    c: Equal(g121,g122)
    c: Equal(g121,g123)
    c: InternalAlignment(g121,g124)
    c: InternalAlignment(g122,g124)
    c: InternalAlignment(g123,g124)
    c: InternalAlignment(g125,g124)
    c: InternalAlignment(g126,g124)
    c: Weight(g127) = 1
    c: Equal(g127,g128)
    c: Equal(g127,g129)
    c: InternalAlignment(g127,g130)
    c: InternalAlignment(g128,g130)
    c: InternalAlignment(g129,g130)
    c: InternalAlignment(g131,g130)
    c: InternalAlignment(g132,g130)
    c: Block(g124)
    c: Block(g130)
    c: Coincident(g133,g124)
    c: Coincident(g133,g130)
    c: Vertical(g133)
    c: Coincident(g134,g130)
    c: Coincident(g134,g67)
    c: Coincident(g135,g67)
    c: Coincident(g135,g124)
    c: Weight(g136) = 1
    c: Equal(g136,g137)
    c: Equal(g136,g138)
    c: InternalAlignment(g136,g139)
    c: InternalAlignment(g137,g139)
    c: InternalAlignment(g138,g139)
    c: InternalAlignment(g140,g139)
    c: InternalAlignment(g141,g139)
    c: Weight(g142) = 1
    c: Equal(g142,g143)
    c: Equal(g142,g144)
    c: InternalAlignment(g142,g145)
    c: InternalAlignment(g143,g145)
    c: InternalAlignment(g144,g145)
    c: InternalAlignment(g146,g145)
    c: InternalAlignment(g147,g145)
    c: Weight(g148) = 1
    c: Equal(g148,g149)
    c: Equal(g148,g150)
    c: InternalAlignment(g148,g151)
    c: InternalAlignment(g149,g151)
    c: InternalAlignment(g150,g151)
    c: InternalAlignment(g152,g151)
    c: InternalAlignment(g153,g151)
    c: Weight(g154) = 1
    c: Equal(g154,g155)
    c: Equal(g154,g156)
    c: InternalAlignment(g154,g157)
    c: InternalAlignment(g155,g157)
    c: InternalAlignment(g156,g157)
    c: InternalAlignment(g158,g157)
    c: InternalAlignment(g159,g157)
    c: Block(g157)
    c: Block(g151)
    c: Block(g145)
    c: Block(g139)
    c: Coincident(g160,g34)
    c: Coincident(g160,g157)
    c: Coincident(g161,g157)
    c: Coincident(g161,g151)
    c: Horizontal(g161)
    c: Coincident(g162,g151)
    c: Coincident(g162,g34)
    c: Vertical(g162)
    c: Coincident(g163,g28)
    c: Coincident(g163,g145)
    c: Vertical(g163)
    c: Coincident(g164,g145)
    c: Coincident(g164,g139)
    c: Horizontal(g164)
    c: Coincident(g165,g139)
    c: Coincident(g165,g28)
    c: Weight(g166) = 1
    c: Equal(g166,g167)
    c: Equal(g166,g168)
    c: InternalAlignment(g166,g169)
    c: InternalAlignment(g167,g169)
    c: InternalAlignment(g168,g169)
    c: InternalAlignment(g170,g169)
    c: InternalAlignment(g171,g169)
    c: Weight(g172) = 1
    c: Equal(g172,g173)
    c: Equal(g172,g174)
    c: InternalAlignment(g172,g175)
    c: InternalAlignment(g173,g175)
    c: InternalAlignment(g174,g175)
    c: InternalAlignment(g176,g175)
    c: InternalAlignment(g177,g175)
    c: Weight(g178) = 1
    c: Equal(g178,g179)
    c: Equal(g178,g180)
    c: InternalAlignment(g178,g181)
    c: InternalAlignment(g179,g181)
    c: InternalAlignment(g180,g181)
    c: InternalAlignment(g182,g181)
    c: InternalAlignment(g183,g181)
    c: Weight(g184) = 1
    c: Equal(g184,g185)
    c: Equal(g184,g186)
    c: InternalAlignment(g184,g187)
    c: InternalAlignment(g185,g187)
    c: InternalAlignment(g186,g187)
    c: InternalAlignment(g188,g187)
    c: InternalAlignment(g189,g187)
    c: Block(g187)
    c: Block(g181)
    c: Block(g175)
    c: Block(g169)
    c: Coincident(g190,g187)
    c: Coincident(g190,g181)
    c: Horizontal(g190)
    c: Coincident(g191,g181)
    c: Coincident(g191,g16)
    c: Vertical(g191)
    c: Coincident(g192,g22)
    c: Coincident(g192,g175)
    c: Vertical(g192)
    c: Coincident(g193,g175)
    c: Coincident(g193,g169)
    c: Horizontal(g193)
    c: Coincident(g194,g169)
    c: Coincident(g194,g22)
    c: Coincident(g195,g16)
    c: Weight(g196) = 1
    c: Equal(g196,g197)
    c: Equal(g196,g198)
    c: InternalAlignment(g196,g199)
    c: InternalAlignment(g197,g199)
    c: InternalAlignment(g198,g199)
    c: InternalAlignment(g200,g199)
    c: InternalAlignment(g201,g199)
    c: Weight(g202) = 1
    c: Equal(g202,g203)
    c: Equal(g202,g204)
    c: InternalAlignment(g202,g205)
    c: InternalAlignment(g203,g205)
    c: InternalAlignment(g204,g205)
    c: InternalAlignment(g206,g205)
    c: InternalAlignment(g207,g205)
    c: Block(g205)
    c: Block(g199)
    c: Coincident(g208,g205)
    c: Coincident(g208,g40)
    c: Coincident(g209,g40)
    c: Coincident(g209,g199)
    c: Coincident(g210,g199)
    c: Coincident(g210,g205)
    c: Vertical(g210)
    c: Weight(g211) = 1
    c: Equal(g211,g212)
    c: Equal(g211,g213)
    c: InternalAlignment(g211,g214)
    c: InternalAlignment(g212,g214)
    c: InternalAlignment(g213,g214)
    c: InternalAlignment(g215,g214)
    c: InternalAlignment(g216,g214)
    c: Weight(g217) = 1
    c: Equal(g217,g218)
    c: Equal(g217,g219)
    c: InternalAlignment(g217,g220)
    c: InternalAlignment(g218,g220)
    c: InternalAlignment(g219,g220)
    c: InternalAlignment(g221,g220)
    c: InternalAlignment(g222,g220)
    c: Block(g220)
    c: Block(g214)
    c: Coincident(g223,g214)
    c: Coincident(g223,g46)
    c: Coincident(g224,g46)
    c: Coincident(g224,g220)
    c: Coincident(g225,g220)
    c: Coincident(g225,g214)
    c: Vertical(g225)
    c: Horizontal(g226)
    c: Block(g226)
    c: Vertical(g227)
    c: Block(g227)
    c: Block(g228)
    c: Weight(g229) = 1
    c: Equal(g229,g230)
    c: Equal(g229,g231)
    c: InternalAlignment(g229,g232)
    c: InternalAlignment(g230,g232)
    c: InternalAlignment(g231,g232)
    c: InternalAlignment(g233,g232)
    c: InternalAlignment(g234,g232)
    c: Weight(g235) = 1
    c: Equal(g235,g236)
    c: Equal(g235,g237)
    c: InternalAlignment(g235,g238)
    c: InternalAlignment(g236,g238)
    c: InternalAlignment(g237,g238)
    c: InternalAlignment(g239,g238)
    c: InternalAlignment(g240,g238)
    c: Weight(g241) = 1
    c: Equal(g241,g242)
    c: Equal(g241,g243)
    c: InternalAlignment(g241,g244)
    c: InternalAlignment(g242,g244)
    c: InternalAlignment(g243,g244)
    c: InternalAlignment(g245,g244)
    c: InternalAlignment(g246,g244)
    c: Weight(g247) = 1
    c: Equal(g247,g248)
    c: Equal(g247,g249)
    c: InternalAlignment(g247,g250)
    c: InternalAlignment(g248,g250)
    c: InternalAlignment(g249,g250)
    c: InternalAlignment(g251,g250)
    c: InternalAlignment(g252,g250)
    c: Block(g232)
    c: Block(g238)
    c: Block(g244)
    c: Block(g250)
    c: Coincident(g253,g238)
    c: Coincident(g253,g232)
    c: Horizontal(g253)
    c: Block(g195)
    c: Weight(g254) = 1
    c: Equal(g254,g255)
    c: Equal(g254,g256)
    c: InternalAlignment(g254,g257)
    c: InternalAlignment(g255,g257)
    c: InternalAlignment(g256,g257)
    c: InternalAlignment(g258,g257)
    c: InternalAlignment(g259,g257)
    c: Weight(g260) = 1
    c: Equal(g260,g261)
    c: Equal(g260,g262)
    c: InternalAlignment(g260,g263)
    c: InternalAlignment(g261,g263)
    c: InternalAlignment(g262,g263)
    c: InternalAlignment(g264,g263)
    c: InternalAlignment(g265,g263)
    c: Weight(g266) = 1
    c: Equal(g266,g267)
    c: Equal(g266,g268)
    c: InternalAlignment(g266,g269)
    c: InternalAlignment(g267,g269)
    c: InternalAlignment(g268,g269)
    c: InternalAlignment(g270,g269)
    c: InternalAlignment(g271,g269)
    c: Weight(g272) = 1
    c: Equal(g272,g273)
    c: Equal(g272,g274)
    c: InternalAlignment(g272,g275)
    c: InternalAlignment(g273,g275)
    c: InternalAlignment(g274,g275)
    c: InternalAlignment(g276,g275)
    c: InternalAlignment(g277,g275)
    c: Block(g257)
    c: Block(g263)
    c: Block(g269)
    c: Block(g275)
    c: Coincident(g278,g269)
    c: Coincident(g278,g275)
    c: Horizontal(g278)
    c: Coincident(g279,g275)
    c: Coincident(g279,g257)
    c: Vertical(g279)
    c: Coincident(g280,g257)
    c: Coincident(g280,g263)
    c: Coincident(g281,g263)
    c: Coincident(g281,g269)
    c: Vertical(g281)
    c: Weight(g282) = 1
    c: Equal(g282,g283)
    c: Equal(g282,g284)
    c: InternalAlignment(g282,g285)
    c: InternalAlignment(g283,g285)
    c: InternalAlignment(g284,g285)
    c: InternalAlignment(g286,g285)
    c: InternalAlignment(g287,g285)
    c: Weight(g288) = 1
    c: Equal(g288,g289)
    c: Equal(g288,g290)
    c: InternalAlignment(g288,g291)
    c: InternalAlignment(g289,g291)
    c: InternalAlignment(g290,g291)
    c: InternalAlignment(g292,g291)
    c: InternalAlignment(g293,g291)
    c: Weight(g294) = 1
    c: Equal(g294,g295)
    c: Equal(g294,g296)
    c: InternalAlignment(g294,g297)
    c: InternalAlignment(g295,g297)
    c: InternalAlignment(g296,g297)
    c: InternalAlignment(g298,g297)
    c: InternalAlignment(g299,g297)
    c: Block(g297)
    c: Block(g291)
    c: Block(g285)
    c: Coincident(g300,g291)
    c: Coincident(g300,g285)
    c: Coincident(g301,g285)
    c: Coincident(g301,g297)
    c: Vertical(g301)
    c: Coincident(g302,g297)
    c: Coincident(g302,g291)
    c: Horizontal(g302)
    c: Weight(g303) = 1
    c: Equal(g303,g304)
    c: InternalAlignment(g303,g305)
    c: InternalAlignment(g304,g305)
    c: InternalAlignment(g306,g305)
    c: InternalAlignment(g307,g305)
    c: Weight(g308) = 1
    c: Equal(g308,g309)
    c: Equal(g308,g310)
    c: InternalAlignment(g308,g311)
    c: InternalAlignment(g309,g311)
    c: InternalAlignment(g310,g311)
    c: InternalAlignment(g312,g311)
    c: InternalAlignment(g313,g311)
    c: Weight(g314) = 1
    c: Equal(g314,g315)
    c: Equal(g314,g316)
    c: InternalAlignment(g314,g317)
    c: InternalAlignment(g315,g317)
    c: InternalAlignment(g316,g317)
    c: InternalAlignment(g318,g317)
    c: InternalAlignment(g319,g317)
    c: Equal(g320,g321)
    c: Equal(g320,g322)
    c: InternalAlignment(g320,g323)
    c: InternalAlignment(g321,g323)
    c: InternalAlignment(g322,g323)
    c: InternalAlignment(g324,g323)
    c: InternalAlignment(g325,g323)
    c: Block(g311)
    c: Block(g317)
    c: Block(g323)
    c: Block(g305)
    c: Coincident(g326,g305)
    c: Coincident(g326,g311)
    c: Horizontal(g326)
    c: Coincident(g327,g311)
    c: Coincident(g327,g317)
    c: Vertical(g327)
    c: Coincident(g328,g317)
    c: Coincident(g328,g323)
    c: Horizontal(g328)
    c: Coincident(g329,g323)
    c: Coincident(g329,g305)
    c: Weight(g330) = 1
    c: Equal(g330,g331)
    c: Equal(g330,g332)
    c: InternalAlignment(g330,g333)
    c: InternalAlignment(g331,g333)
    c: InternalAlignment(g332,g333)
    c: InternalAlignment(g334,g333)
    c: InternalAlignment(g335,g333)
    c: Weight(g336) = 1
    c: Equal(g336,g337)
    c: Equal(g336,g338)
    c: InternalAlignment(g336,g339)
    c: InternalAlignment(g337,g339)
    c: InternalAlignment(g338,g339)
    c: InternalAlignment(g340,g339)
    c: InternalAlignment(g341,g339)
    c: Weight(g342) = 1
    c: Equal(g342,g343)
    c: Equal(g342,g344)
    c: InternalAlignment(g342,g345)
    c: InternalAlignment(g343,g345)
    c: InternalAlignment(g344,g345)
    c: InternalAlignment(g346,g345)
    c: InternalAlignment(g347,g345)
    c: Block(g345)
    c: Block(g339)
    c: Block(g333)
    c: Coincident(g348,g345)
    c: Coincident(g348,g339)
    c: Horizontal(g348)
    c: Coincident(g349,g339)
    c: Coincident(g349,g333)
    c: Vertical(g349)
    c: Coincident(g350,g333)
    c: Coincident(g350,g345)
FEATURE [Sketcher::SketchObject] Sketch001
  FullyConstrained = true
  MapMode = 4
  Placement = pos=(0,0,0) rot=(0.57735,0.57735,0.57735;2.0944rad)
  Support = -> [Sketch]
  sketch-geometry (46):
    g0: BSplineCurve PolesCount=3 KnotsCount=2 Degree=2 IsPeriodic=0
    g1: ArcOfCircle CenterX=73.1223 CenterY=-32.291 CenterZ=0 NormalX=0 NormalY=0 NormalZ=1 AngleXU=0 Radius=13 StartAngle=5.92268 EndAngle=9.06428
    g2: ArcOfCircle CenterX=66.7816 CenterY=-49.1439 CenterZ=0 NormalX=0 NormalY=0 NormalZ=1 AngleXU=0 Radius=13 StartAngle=2.78068 EndAngle=5.92131
    g3: ArcOfCircle CenterX=55.9263 CenterY=-78.1807 CenterZ=0 NormalX=0 NormalY=0 NormalZ=1 AngleXU=0 Radius=13 StartAngle=5.92268 EndAngle=9.06428
    g4: ArcOfCircle CenterX=49.5884 CenterY=-95.0342 CenterZ=0 NormalX=0 NormalY=0 NormalZ=1 AngleXU=0 Radius=13 StartAngle=2.78068 EndAngle=5.92131
    g5: ArcOfCircle CenterX=38.7206 CenterY=-124.067 CenterZ=0 NormalX=0 NormalY=0 NormalZ=1 AngleXU=0 Radius=13 StartAngle=5.92268 EndAngle=9.06428
    g6: ArcOfCircle CenterX=32.3875 CenterY=-140.92 CenterZ=0 NormalX=0 NormalY=0 NormalZ=1 AngleXU=0 Radius=13 StartAngle=2.78068 EndAngle=5.92131
    g7: ArcOfCircle CenterX=21.4715 CenterY=-169.934 CenterZ=0 NormalX=0 NormalY=0 NormalZ=1 AngleXU=0 Radius=13 StartAngle=5.92268 EndAngle=9.06428
    g8: ArcOfCircle CenterX=15.1336 CenterY=-186.787 CenterZ=0 NormalX=0 NormalY=0 NormalZ=1 AngleXU=0 Radius=13 StartAngle=2.78068 EndAngle=5.92131
    g9-g12: Circle x4 (B-spline internal-alignment scaffolding for g13; pole/knot coordinates omitted)
    g13: BSplineCurve PolesCount=4 KnotsCount=2 Degree=3 IsPeriodic=0
    g14: GeomPoint X=28.8094 Y=-19.0875 Z=0
    g15: GeomPoint X=47.0443 Y=-50.4712 Z=0
    g16: Circle CenterX=53.5586 CenterY=-23.2695 CenterZ=0 NormalX=0 NormalY=0 NormalZ=1 AngleXU=0 Radius=3.24518
    g17: Circle CenterX=-195.441 CenterY=-127.082 CenterZ=0 NormalX=0 NormalY=0 NormalZ=1 AngleXU=0 Radius=1
    g18: Circle CenterX=-8.24091 CenterY=-197.481 CenterZ=0 NormalX=0 NormalY=0 NormalZ=1 AngleXU=0 Radius=1
    g19: Circle CenterX=12.8789 CenterY=-141.321 CenterZ=0 NormalX=0 NormalY=0 NormalZ=1 AngleXU=0 Radius=1
    g20: BSplineCurve PolesCount=3 KnotsCount=2 Degree=2 IsPeriodic=0
    g21: GeomPoint X=-195.441 Y=-127.082 Z=0
    g22: GeomPoint X=12.8789 Y=-141.321 Z=0
    g23: Circle CenterX=-12.8016 CenterY=-179.036 CenterZ=0 NormalX=0 NormalY=0 NormalZ=1 AngleXU=0 Radius=10.5072
    g24: Circle CenterX=0.933922 CenterY=-166.43 CenterZ=0 NormalX=0 NormalY=0 NormalZ=1 AngleXU=0 Radius=3.26661
    g25: Circle CenterX=-33.5518 CenterY=-176.44 CenterZ=0 NormalX=0 NormalY=0 NormalZ=1 AngleXU=0 Radius=5.64388
    g26: Circle CenterX=-47.2366 CenterY=-173.859 CenterZ=0 NormalX=0 NormalY=0 NormalZ=1 AngleXU=0 Radius=3.01653
    g27: Circle CenterX=-56.2595 CenterY=-171.456 CenterZ=0 NormalX=0 NormalY=0 NormalZ=1 AngleXU=0 Radius=2.12826
    g28: ArcOfCircle CenterX=51.2151 CenterY=-198.473 CenterZ=0 NormalX=0 NormalY=0 NormalZ=1 AngleXU=0 Radius=20 StartAngle=2.78189 EndAngle=4.35269
    g29: LineSegment StartX=32.4951 StartY=-191.433 StartZ=0 EndX=94.6578 EndY=-26.1352 EndZ=0
    g30: LineSegment StartX=43.1192 StartY=-220.001 StartZ=0 EndX=-196.497 EndY=-129.89 EndZ=0
    g31: LineSegment StartX=43.1192 StartY=-220.001 StartZ=0 EndX=44.1752 EndY=-217.193 EndZ=0
    g32: LineSegment StartX=117.223 StartY=-19.0875 StartZ=0 EndX=117.223 EndY=-16.0875 EndZ=0
    g33: LineSegment StartX=117.223 StartY=-16.0875 StartZ=0 EndX=17.2232 EndY=-16.0875 EndZ=0
    g34: LineSegment StartX=17.2232 StartY=-16.0875 StartZ=0 EndX=17.2232 EndY=-19.0875 EndZ=0
    g35: LineSegment StartX=28.8094 StartY=-19.0875 StartZ=0 EndX=17.2232 EndY=-19.0875 EndZ=0
    g36: LineSegment StartX=47.0443 StartY=-50.4712 StartZ=0 EndX=12.8789 EndY=-141.321 EndZ=0
    g37: LineSegment StartX=-195.441 StartY=-127.082 StartZ=0 EndX=-196.497 EndY=-129.89 EndZ=0
    g38: LineSegment StartX=85.2866 StartY=-36.8766 StartZ=0 EndX=78.9396 EndY=-53.7463 EndZ=0
    g39: LineSegment StartX=60.9579 StartY=-27.7053 StartZ=0 EndX=54.6191 EndY=-44.5532 EndZ=0
    g40: LineSegment StartX=68.0907 StartY=-82.7664 StartZ=0 EndX=61.7465 EndY=-99.6365 EndZ=0
    g41: LineSegment StartX=43.7619 StartY=-73.595 StartZ=0 EndX=37.426 EndY=-90.4435 EndZ=0
    g42: LineSegment StartX=50.885 StartY=-128.652 StartZ=0 EndX=44.5456 EndY=-145.522 EndZ=0
    g43: LineSegment StartX=26.5562 StartY=-119.481 StartZ=0 EndX=20.2251 EndY=-136.329 EndZ=0
    g44: LineSegment StartX=9.3071 StartY=-165.349 StartZ=0 EndX=2.97115 EndY=-182.197 EndZ=0
    g45: LineSegment StartX=33.6358 StartY=-174.52 StartZ=0 EndX=27.2917 EndY=-191.39 EndZ=0
  constraints (71):
    c: Block(g0)
    c: Block(g1)
    c: Block(g2)
    c: Block(g4)
    c: Block(g3)
    c: Block(g6)
    c: Block(g5)
    c: Block(g8)
    c: Block(g7)
    c: Weight(g9) = 1
    c: Equal(g9,g10)
    c: Equal(g9,g11)
    c: Equal(g9,g12)
    c: InternalAlignment(g9-g12 -> g13) x4
    c: InternalAlignment(g14,g13)
    c: InternalAlignment(g15,g13)
    c: Block(g16)
    c: Weight(g17) = 1
    c: Equal(g17,g18)
    c: Equal(g17,g19)
    c: InternalAlignment(g17,g20)
    c: InternalAlignment(g18,g20)
    c: InternalAlignment(g19,g20)
    c: InternalAlignment(g21,g20)
    c: InternalAlignment(g22,g20)
    c: Block(g20)
    c: Block(g23)
    c: Block(g24)
    c: Block(g25)
    c: Block(g26)
    c: Block(g27)
    c: Block(g28)
    c: Coincident(g29,g28)
    c: Coincident(g29,g0)
    c: Block(g13)
    c: Coincident(g31,g30)
    c: Coincident(g31,g28)
    c: Block(g31)
    c: Coincident(g32,g0)
    c: Vertical(g32)
    c: Coincident(g33,g32)
    c: Horizontal(g33)
    c: Coincident(g34,g33)
    c: Vertical(g34)
    c: Block(g33)
    c: Coincident(g35,g13)
    c: Coincident(g35,g34)
    c: Horizontal(g35)
    c: Coincident(g36,g13)
    c: Coincident(g36,g20)
    c: Coincident(g37,g20)
    c: Coincident(g37,g30)
    c: Block(g30)
    c: Coincident(g38,g1)
    c: Coincident(g38,g2)
    c: Coincident(g39,g1)
    c: Coincident(g39,g2)
    c: Coincident(g40,g3)
    c: Coincident(g40,g4)
    c: Coincident(g41,g3)
    c: Coincident(g41,g4)
    c: Coincident(g42,g5)
    c: Coincident(g42,g6)
    c: Coincident(g43,g5)
    c: Coincident(g43,g6)
    c: Coincident(g44,g7)
    c: Coincident(g44,g8)
    c: Coincident(g45,g7)
    c: Coincident(g45,g8)
    c: Distance(g30) = 256
    c: Distance(g33) = 100
FEATURE [Part::Extrusion] Extrude002
  Base = -> Sketch001
  Dir = (1,0,0)
  DirMode = 2
  FaceMakerClass = Part::FaceMakerBullseye
  LengthFwd = 8
  LengthRev = 0
  Solid = true
  Symmetric = false
FEATURE [Sketcher::SketchObject] Sketch002
  FullyConstrained = true
  sketch-geometry (20):
    g0: LineSegment StartX=-2.77179 StartY=-200.304 StartZ=0 EndX=5.22821 EndY=-200.304 EndZ=0
    g1: LineSegment StartX=5.22821 StartY=-200.304 StartZ=0 EndX=5.22821 EndY=-197.304 EndZ=0
    g2: LineSegment StartX=-2.77179 StartY=-200.304 StartZ=0 EndX=-2.77179 EndY=-197.304 EndZ=0
    g3: LineSegment StartX=5.22821 StartY=-197.304 StartZ=0 EndX=8.22821 EndY=-197.304 EndZ=0
    g4: LineSegment StartX=-2.77179 StartY=-197.304 StartZ=0 EndX=-5.77179 EndY=-197.304 EndZ=0
    g5: LineSegment StartX=19.2282 StartY=-203.304 StartZ=0 EndX=19.2282 EndY=-206.304 EndZ=0
    g6: LineSegment StartX=-16.7718 StartY=-203.304 StartZ=0 EndX=-16.7718 EndY=-206.304 EndZ=0
    g7: LineSegment StartX=-16.7718 StartY=-206.304 StartZ=0 EndX=19.2282 EndY=-206.304 EndZ=0
    g8: Circle CenterX=-16.7718 CenterY=-203.304 CenterZ=0 NormalX=0 NormalY=0 NormalZ=1 AngleXU=0 Radius=1
    g9: Circle CenterX=-5.77179 CenterY=-203.304 CenterZ=0 NormalX=0 NormalY=0 NormalZ=1 AngleXU=0 Radius=1
    g10: Circle CenterX=-5.77179 CenterY=-197.304 CenterZ=0 NormalX=0 NormalY=0 NormalZ=1 AngleXU=0 Radius=1
    g11: BSplineCurve PolesCount=3 KnotsCount=2 Degree=2 IsPeriodic=0
    g12: GeomPoint X=-16.7718 Y=-203.304 Z=0
    g13: GeomPoint X=-5.77179 Y=-197.304 Z=0
    g14: Circle CenterX=19.2282 CenterY=-203.304 CenterZ=0 NormalX=0 NormalY=0 NormalZ=1 AngleXU=0 Radius=1
    g15: Circle CenterX=8.22821 CenterY=-203.304 CenterZ=0 NormalX=0 NormalY=0 NormalZ=1 AngleXU=0 Radius=1
    g16: Circle CenterX=8.22821 CenterY=-197.304 CenterZ=0 NormalX=0 NormalY=0 NormalZ=1 AngleXU=0 Radius=1
    g17: BSplineCurve PolesCount=3 KnotsCount=2 Degree=2 IsPeriodic=0
    g18: GeomPoint X=19.2282 Y=-203.304 Z=0
    g19: GeomPoint X=8.22821 Y=-197.304 Z=0
  constraints (41):
    c: Horizontal(g0)
    c: Distance(g0) = 8
    c: Coincident(g1,g0)
    c: Vertical(g1)
    c: Distance(g1) = 3
    c: Coincident(g2,g0)
    c: Vertical(g2)
    c: Distance(g2) = 3
    c: Coincident(g3,g1)
    c: Horizontal(g3)
    c: Distance(g3) = 3
    c: Coincident(g4,g2)
    c: Horizontal(g4)
    c: Distance(g4) = 3
    c: Vertical(g5)
    c: Vertical(g6)
    c: Coincident(g7,g6)
    c: Coincident(g7,g5)
    c: Weight(g8) = 1
    c: Equal(g8,g9)
    c: Equal(g8,g10)
    c: Coincident(g11,g4)
    c: InternalAlignment(g8,g11)
    c: InternalAlignment(g9,g11)
    c: InternalAlignment(g10,g11)
    c: InternalAlignment(g12,g11)
    c: InternalAlignment(g13,g11)
    c: Coincident(g17,g5)
    c: Weight(g14) = 1
    c: Equal(g14,g15)
    c: Equal(g14,g16)
    c: Coincident(g17,g3)
    c: InternalAlignment(g14,g17)
    c: InternalAlignment(g15,g17)
    c: InternalAlignment(g16,g17)
    c: InternalAlignment(g18,g17)
    c: InternalAlignment(g19,g17)
    c: Block(g7)
    c: Block(g17)
    c: Block(g11)
    c: Block(g6)
FEATURE [Part::Extrusion] Extrude003
  Base = -> Sketch002
  Dir = (0,0,1)
  DirMode = 2
  FaceMakerClass = Part::FaceMakerBullseye
  LengthFwd = 260
  LengthRev = 0
  Solid = true
  Symmetric = false
FEATURE [Part::Extrusion] Extrude
  Base = -> Sketch
  Dir = (0,0,1)
  DirMode = 2
  FaceMakerClass = Part::FaceMakerBullseye
  LengthFwd = 14
  LengthRev = 0
  Solid = true
  Symmetric = false
